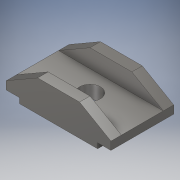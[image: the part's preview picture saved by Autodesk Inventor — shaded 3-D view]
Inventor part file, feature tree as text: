
AUTODESK INVENTOR PART (.ipt)
format: ipt  version: 2019 (Build 230136000, 136)  size: 140,288 bytes
history: native  units: in
note: dims shown in document units (in); Inventor stores cm internally (conversion verified against a paired STEP export)
features: extrude x3, sketch x3, chamfer x1, plane x1, projected_geometry x1
ambient origin geometry x8: Origin, YZ Plane, XZ Plane, XY Plane, X Axis, Y Axis, Z Axis, Center Point
bodies: Solid1 (feature_tree)
feature tree (9):
  extrude  "Extrusion1"  Depth=1.5in
  chamfer  "Chamfer5"  Distance=0.25in
  plane  "Work Plane1"
  extrude  "Extrusion5"  Depth=0.25in
  extrude  "Extrusion6"  Depth=3.0in TaperAngle=0.0deg
  sketch  "Sketch1"  dims[d0=5.0in d1=1.5in]
  sketch  "Sketch8"  dims[d2=0.635in]
  sketch  "Sketch9"  dims[d3=0.635in d4=0.25in d5=0.25in d6=3.0in d7=0.0in d31=1.5in d32=0.125in d33=30.0deg d34=90.0deg d35=0.5in d36=0.5in d38=10.0in d39=0.0in d40=1.0in d41=10.0in d42=0.0in]
  projected_geometry  "Projected Loop3"
